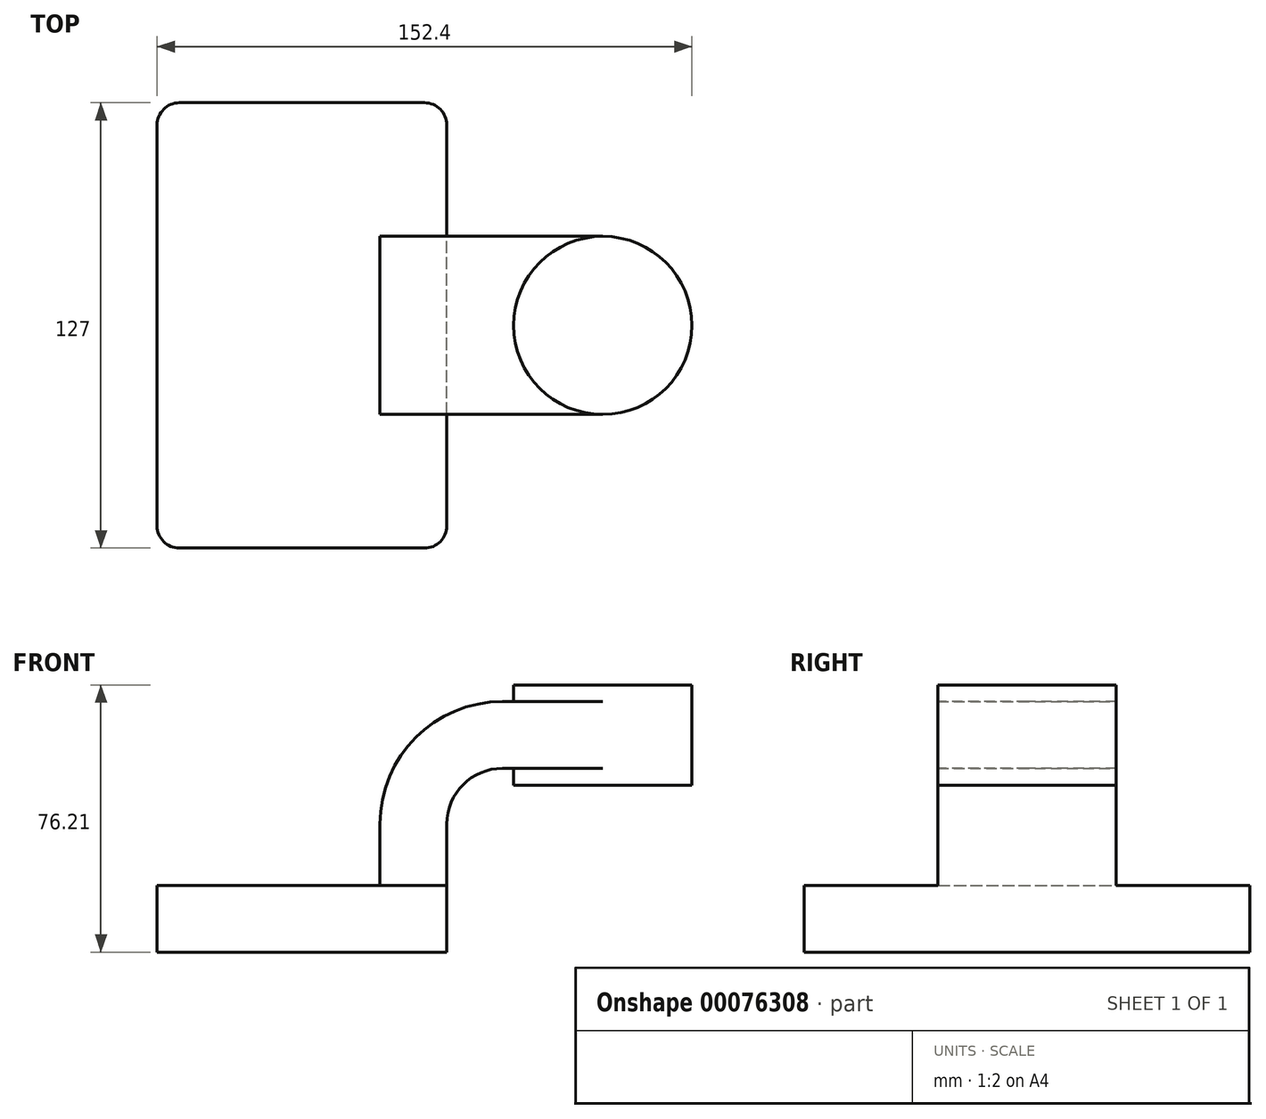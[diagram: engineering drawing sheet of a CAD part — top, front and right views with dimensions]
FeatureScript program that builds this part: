
annotation { "Feature Type Name" : "Feature", "Feature Type Description" : "" }
export const myFeature = defineFeature(function(context is Context, id is Id, definition is map)
    precondition{}
    {
        {
            var Q0;
            Q0=qCreatedBy(makeId("Front.planeOp"),FACE);
            var sketch = newSketch(context, id + "F0", { "sketchPlane" : qUnion([Q0])});
            skLineSegment(sketch, "E0.bottom", {"start": v(-41.28, 9.52) * mm, "end": v(41.27, 9.53) * mm});
            skLineSegment(sketch, "E0.top", {"start": v(-41.27, -9.53) * mm, "end": v(41.28, -9.53) * mm});
            skLineSegment(sketch, "E0.left", {"start": v(-41.28, 9.52) * mm, "end": v(-41.27, -9.53) * mm});
            skLineSegment(sketch, "E0.right", {"start": v(41.27, 9.53) * mm, "end": v(41.28, -9.52) * mm});
            skPoint(sketch, "E0.middle", {"position": v(0, 0) * mm});
            skLineSegment(sketch, "E1.bottom", {"start": v(60.32, 38.1) * mm, "end": v(111.12, 38.1) * mm});
            skLineSegment(sketch, "E1.top", {"start": v(60.32, 66.68) * mm, "end": v(111.12, 66.68) * mm});
            skLineSegment(sketch, "E1.left", {"start": v(60.32, 38.1) * mm, "end": v(60.32, 66.68) * mm});
            skLineSegment(sketch, "E1.right", {"start": v(111.12, 38.1) * mm, "end": v(111.12, 66.68) * mm});
            skPoint(sketch, "E1.middle", {"position": v(85.72, 52.39) * mm});
            skLineSegment(sketch, "E2", {"start": v(41.27, 9.53) * mm, "end": v(41.27, 27) * mm});
            skArc(sketch, "E3", {"start": v(41.27, 27) * mm, "mid": v(45.92, 38.23) * mm, "end": v(57.15, 42.88) * mm});
            skLineSegment(sketch, "E4", {"start": v(57.15, 42.88) * mm, "end": v(85.72, 42.88) * mm});
            skLineSegment(sketch, "E5.0", {"start": v(57.15, 61.93) * mm, "end": v(85.72, 61.93) * mm});
            skArc(sketch, "E5.1", {"start": v(22.22, 27) * mm, "mid": v(32.45, 51.7) * mm, "end": v(57.15, 61.93) * mm});
            skLineSegment(sketch, "E5.2", {"start": v(22.22, 9.53) * mm, "end": v(22.22, 27) * mm});
            skLineSegment(sketch, "E6", {"start": v(85.72, 38.1) * mm, "end": v(85.72, 66.68) * mm});
            skFitSpline(sketch, "E7", {"points": [v(-41.28, 9.53) * mm, v(57.15, 61.93) * mm], "startDerivative": vector(1.74, 99.51) * mm, "endDerivative": vector(137.82, -0.44) * mm});
            skSolve(sketch);
        }
        {
            var Q0;
            Q0=makeQuery(id+"F0.imprint","IMPRINT",FACE,{"disambiguationData":[TD([[makeQuery(id+"F0.imprint","IMPRINT",EDGE,{"derivedFrom":sQuery(id+"F0.wireOp",EDGE,"E0.top")}),1.0]])]});
            extrude(context, id + "F1", {"entities" : qUnion([Q0]), "endBound" : BoundingType.SYMMETRIC, "depth" : 127 * mm});
        }
        {
            var Q0;
            {var subQ1=sQuery(id+"F0.wireOp",EDGE,"E2");Q0=makeQuery(id+"F0.imprint","IMPRINT",FACE,{"disambiguationData":[TD([[makeQuery(id+"F0.imprint","IMPRINT",EDGE,{"derivedFrom":subQ1}),1.0]])]});}
            var Q1;
            {var subQ0=sQuery(id+"F0.wireOp",EDGE,"E4");var subQ1=sQuery(id+"F0.wireOp",EDGE,"E1.left");var subQ2=makeQuery(id+"F0.imprint","INTERSECT",VERTEX,{"derivedFrom":[subQ1,subQ0]});Q1=makeQuery(id+"F0.imprint","IMPRINT",FACE,{"disambiguationData":[TD([[makeQuery(id+"F0.imprint","IMPRINT",EDGE,{"disambiguationData":[TD([[subQ2,-1.0]])],"derivedFrom":subQ1}),-1.0]])]});}
            extrude(context, id + "F2", {"entities" : qUnion([Q0, Q1]), "operationType" : NewBodyOperationType.ADD, "endBound" : BoundingType.SYMMETRIC, "depth" : 50.8 * mm});
        }
        {
            var Q0;
            Q0=makeQuery(id+"F0.imprint","IMPRINT",FACE,{"disambiguationData":[TD([[makeQuery(id+"F0.imprint","IMPRINT",EDGE,{"derivedFrom":sQuery(id+"F0.wireOp",EDGE,"E5.1")}),1.0]])]});
            extrude(context, id + "F3", {"entities" : qUnion([Q0]), "operationType" : NewBodyOperationType.ADD, "endBound" : BoundingType.SYMMETRIC, "depth" : 15.88 * mm});
        }
        {
            var Q0;
            {var subQ0=sQuery(id+"F0.wireOp",EDGE,"E1.right");Q0=makeQuery(id+"F0.imprint","IMPRINT",FACE,{"disambiguationData":[TD([[makeQuery(id+"F0.imprint","IMPRINT",EDGE,{"derivedFrom":subQ0}),1.0]])]});}
            var Q1;
            Q1=sQuery(id+"F0.wireOp",EDGE,"E6");
            revolve(context, id + "F4", {"operationType" : NewBodyOperationType.ADD, "entities" : qUnion([Q0]), "axis" : qUnion([Q1]), "revolveType" : RevolveType.FULL});
        }
        {
            var Q0;
            Q0=makeQuery(id+"F1.opExtrude","CAP_EDGE",EDGE,{"disambiguationData":[OSD([sQuery(id+"F0.wireOp",EDGE,"E0.left")])],"isStart":false});
            var Q1;
            Q1=makeQuery(id+"F1.opExtrude","CAP_EDGE",EDGE,{"disambiguationData":[OSD([sQuery(id+"F0.wireOp",EDGE,"E0.right")])],"isStart":false});
            var Q2;
            Q2=makeQuery(id+"F1.opExtrude","CAP_EDGE",EDGE,{"disambiguationData":[OSD([sQuery(id+"F0.wireOp",EDGE,"E0.right")])],"isStart":true});
            var Q3;
            Q3=makeQuery(id+"F1.opExtrude","CAP_EDGE",EDGE,{"disambiguationData":[OSD([sQuery(id+"F0.wireOp",EDGE,"E0.left")])],"isStart":true});
            fillet(context, id + "F5", {"entities" : qUnion([Q0, Q1, Q2, Q3]), "radius" : 6.35 * mm, "tangentPropagation" : true, "allowEdgeOverflow" : false});
        }
    });
